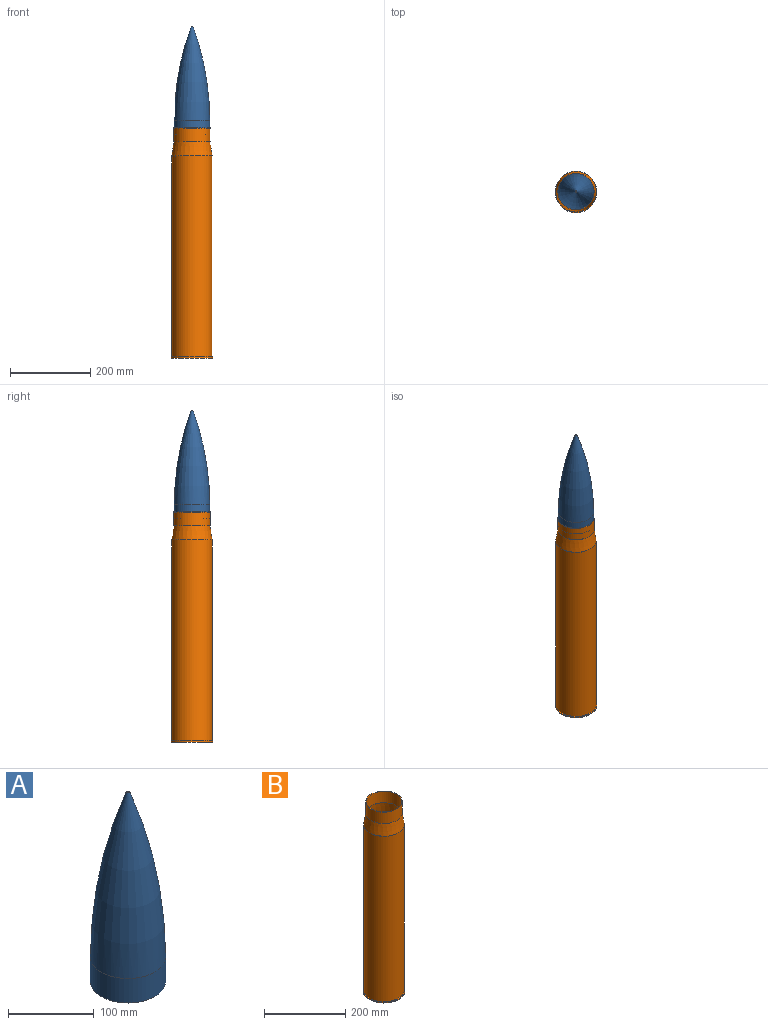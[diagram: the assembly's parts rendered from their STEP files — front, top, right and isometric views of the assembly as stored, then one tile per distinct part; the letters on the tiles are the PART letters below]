
ASSEMBLY  parts=2 mates=1
PART A: 4 faces, bbox 88x88x270.8 mm
  f0: plane 88x88mm, normal (0,0,-1), area 6082.1mm2, adj f1
  f1: cylinder r=44mm len=88mm, axis (0,0,1), area 9676.1mm2, adj f0,f2
  f2: revolved ~235.82x88mm, area 45297.1mm2, adj f1,f3
  f3: plane 4x4mm, normal (0,0,1), area 12.6mm2, adj f2
PART B: 13 faces, bbox 103x103x572 mm
  f0: plane 101x101mm, normal (0,0,1), area 8011.8mm2, adj f11
  f1: plane 103x103mm, normal (0,0,-1), area 8332.3mm2, adj f2
  f2: cylinder r=51.5mm len=103mm, axis (0,0,-1), area 970.8mm2, adj f1,f3
  f3: plane 103x103mm, normal (0,0,1), area 478.3mm2, adj f2,f4
  f4: cylinder r=50mm len=499.07mm, axis (0,0,-1), area 156787.8mm2, adj f3,f5
  f5: cone r=50mm half-angle=8.1deg, axis (0,0,-1), area 10551.8mm2, adj f4,f6
  f6: cylinder r=45mm len=90mm, axis (0,0,-1), area 9734.6mm2, adj f5,f12
  f7: cylinder r=44mm len=88mm, axis (0,0,-1), area 9537.9mm2, adj f8,f12
  f8: cone r=49mm half-angle=8.1deg, axis (0,0,-1), area 10329.7mm2, adj f7,f9
  f9: cylinder r=49mm len=500mm, axis (0,0,-1), area 153938mm2, adj f8,f10
  f10: plane 101x101mm, normal (0,0,-1), area 468.9mm2, adj f9,f11
  f11: cylinder r=50.5mm len=101mm, axis (0,0,-1), area 317.3mm2, adj f0,f10
  f12: torus R=44.5mm, axis (0,0,-1), area 439.2mm2, adj f6,f7
PLACE A t=(-315.59,88.82,271.12)mm
PLACE B t=(-315.59,88.82,-282.13)mm
MATE fastened B.f2 <-> A.f1  axis (0,0,-1) through (-315.59,88.82,271.12)mm
